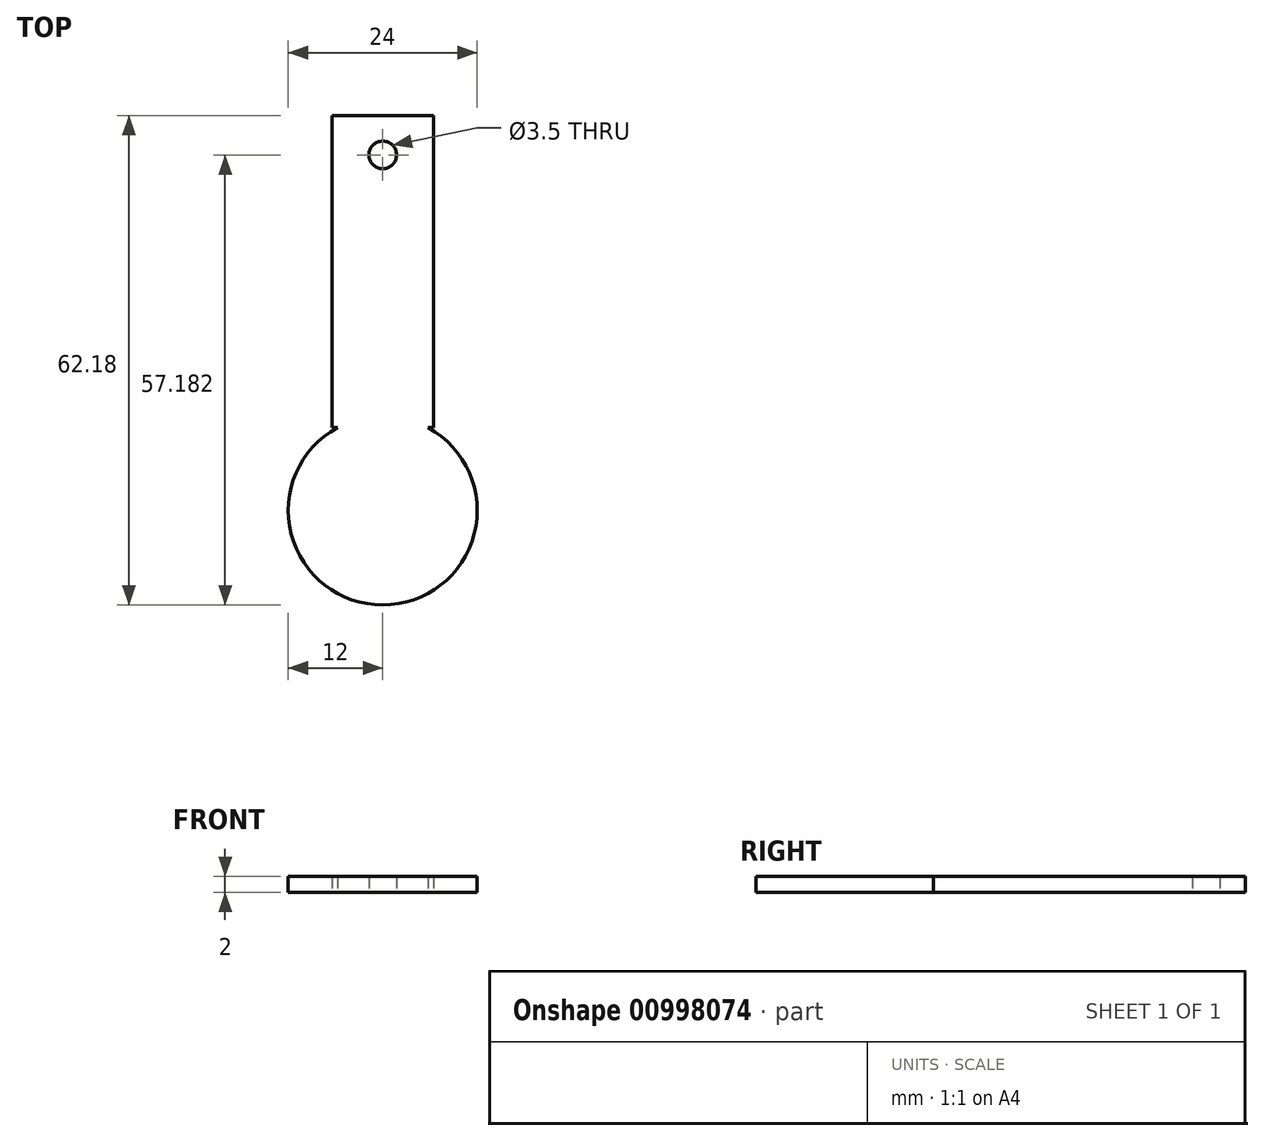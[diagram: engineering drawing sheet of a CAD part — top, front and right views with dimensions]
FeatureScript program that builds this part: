
annotation { "Feature Type Name" : "Feature", "Feature Type Description" : "" }
export const myFeature = defineFeature(function(context is Context, id is Id, definition is map)
    precondition{}
    {
        {
            var Q0;
            Q0=qCreatedBy(makeId("Top.planeOp"),FACE);
            var sketch = newSketch(context, id + "F0", { "sketchPlane" : qUnion([Q0])});
            skCircle(sketch, "E0", {"center": v(0, 0) * mm, "radius": 12 * mm});
            skLineSegment(sketch, "E1.bottom", {"start": v(6.43, 10.52) * mm, "end": v(-6.43, 10.52) * mm});
            skLineSegment(sketch, "E1.top", {"start": v(6.43, 50.18) * mm, "end": v(-6.43, 50.18) * mm});
            skLineSegment(sketch, "E1.left", {"start": v(6.43, 10.52) * mm, "end": v(6.43, 50.18) * mm});
            skLineSegment(sketch, "E1.right", {"start": v(-6.43, 10.52) * mm, "end": v(-6.43, 50.18) * mm});
            skPoint(sketch, "E1.middle", {"position": v(0, 30.35) * mm});
            skCircle(sketch, "E2", {"center": v(0, 45.18) * mm, "radius": 1.75 * mm});
            skSolve(sketch);
        }
        {
            var Q0;
            Q0 = qSketchRegion(id + "F0", true);
            extrude(context, id + "F1", {"entities" : qUnion([Q0]), "depth" : 2 * mm, "offsetDistance" : 25 * mm});
        }
    });
